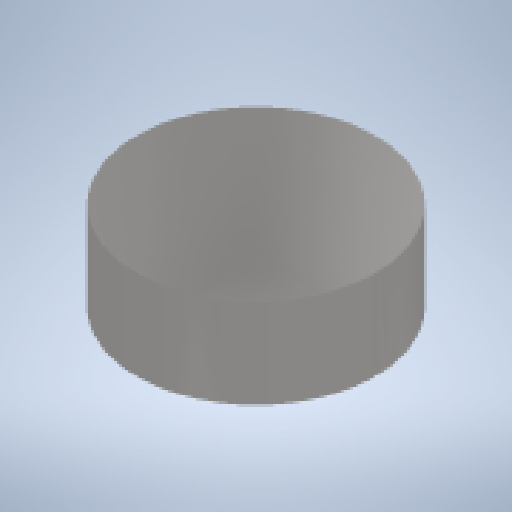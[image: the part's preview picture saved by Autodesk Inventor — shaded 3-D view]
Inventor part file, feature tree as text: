
AUTODESK INVENTOR PART (.ipt)
format: ipt  version: 2024 (Build 280153000, 153)  size: 142,336 bytes
history: native  units: mm
features: sketch x2, other x1, extrude x1, hole x1
ambient origin geometry x8: Origin, YZ Plane, XZ Plane, XY Plane, X Axis, Y Axis, Z Axis, Center Point
bodies: Body1 (feature_tree)
feature tree (5):
  other  "ソリッド1"
  extrude  "押し出し1"  Depth=8.0mm
  hole  "穴1"  [1 undecoded]
  sketch  "スケッチ1"
  sketch  "スケッチ2"
note: 1 required parameter value undecoded (feature->parameter linkage not recoverable at this tier; creation-order binding heuristic only, values carry confidence <= 0.55)
